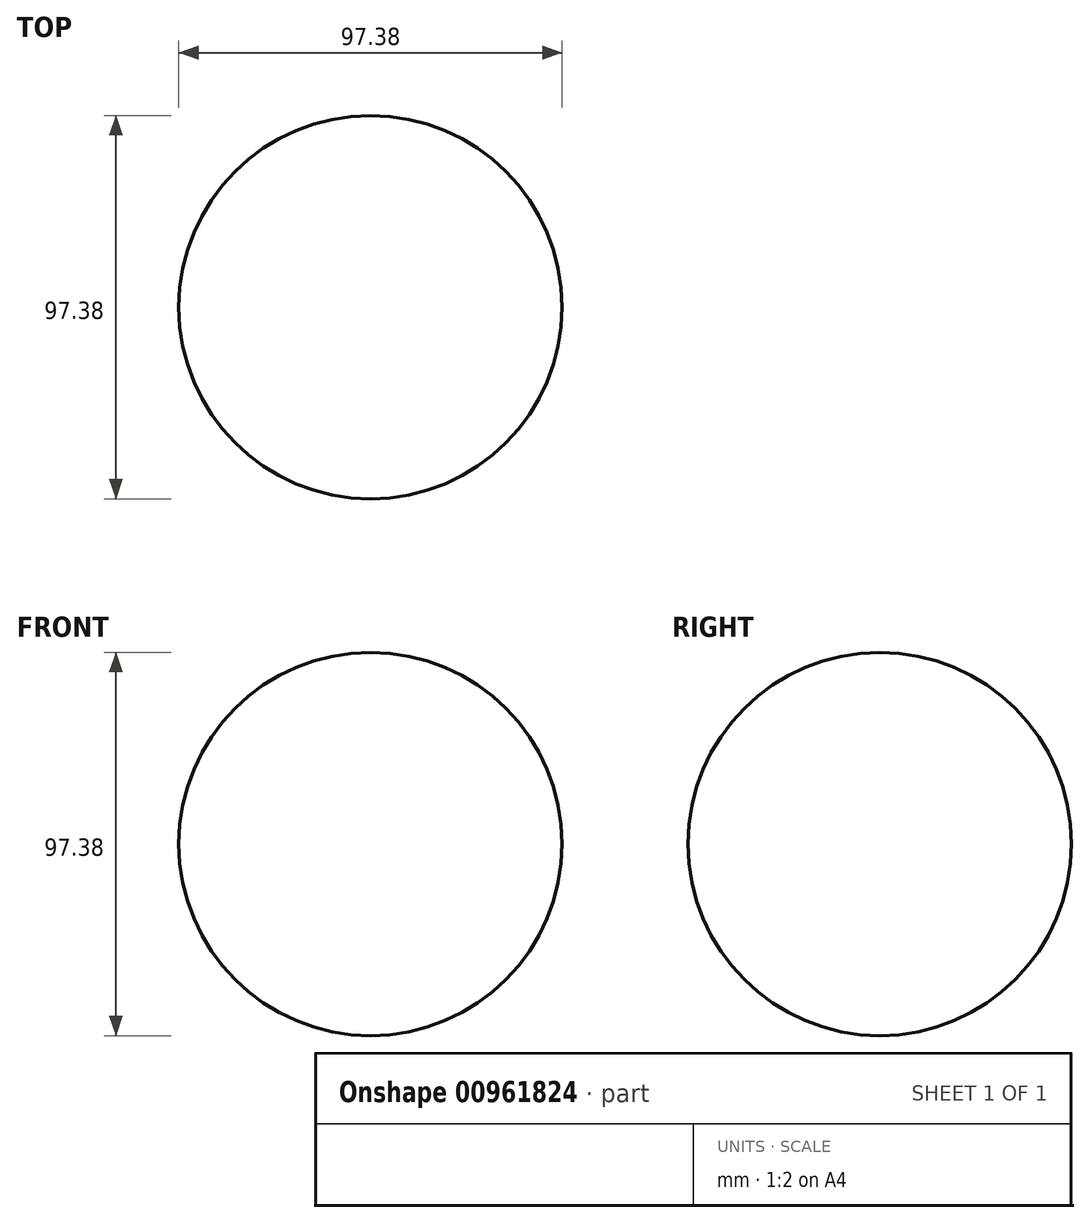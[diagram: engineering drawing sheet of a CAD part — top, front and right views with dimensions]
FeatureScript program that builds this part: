
annotation { "Feature Type Name" : "Feature", "Feature Type Description" : "" }
export const myFeature = defineFeature(function(context is Context, id is Id, definition is map)
    precondition{}
    {
        {
            var Q0;
            Q0=qCreatedBy(makeId("Front.planeOp"),FACE);
            var sketch = newSketch(context, id + "F0", { "sketchPlane" : qUnion([Q0])});
            skArc(sketch, "E0", {"start": v(0, -48.69) * mm, "mid": v(48.69, 0) * mm, "end": v(0, 48.69) * mm});
            skLineSegment(sketch, "E1", {"start": v(0, -48.69) * mm, "end": v(0, 48.69) * mm});
            skSolve(sketch);
        }
        {
            var Q0;
            Q0 = qSketchRegion(id + "F0", true);
            var Q1;
            Q1=sQuery(id+"F0.wireOp",EDGE,"E1");
            revolve(context, id + "F1", {"surfaceOperationType" : NewSurfaceOperationType.NEW, "entities" : qUnion([Q0]), "axis" : qUnion([Q1]), "revolveType" : RevolveType.FULL});
        }
    });
